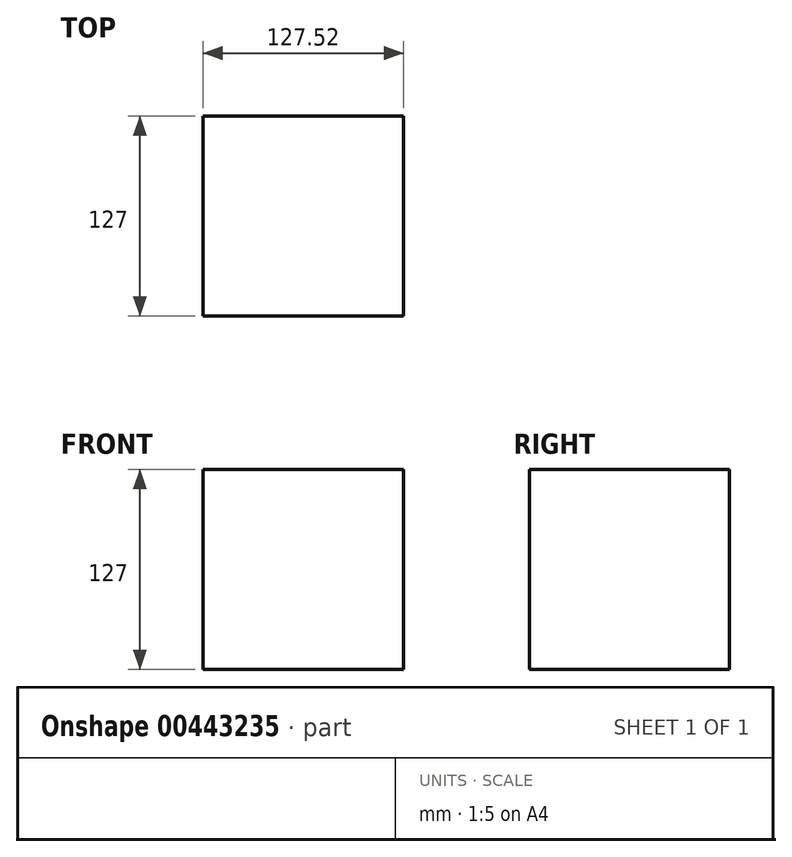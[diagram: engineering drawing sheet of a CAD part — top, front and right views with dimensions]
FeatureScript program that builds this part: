
annotation { "Feature Type Name" : "Feature", "Feature Type Description" : "" }
export const myFeature = defineFeature(function(context is Context, id is Id, definition is map)
    precondition{}
    {
        {
            var Q0;
            Q0=qCreatedBy(makeId("Front.planeOp"),FACE);
            var sketch = newSketch(context, id + "F0", { "sketchPlane" : qUnion([Q0])});
            skLineSegment(sketch, "E0", {"start": v(-63.76, 63.5) * mm, "end": v(63.76, 63.5) * mm});
            skLineSegment(sketch, "E1", {"start": v(63.76, -63.5) * mm, "end": v(-63.76, -63.5) * mm});
            skLineSegment(sketch, "E2", {"start": v(-63.76, 63.5) * mm, "end": v(-63.76, -63.5) * mm});
            skLineSegment(sketch, "E3", {"start": v(63.76, 63.5) * mm, "end": v(63.76, -63.5) * mm});
            skSolve(sketch);
        }
        {
            var Q0;
            Q0=makeQuery(id+"F0.imprint","IMPRINT",FACE,{"disambiguationData":[TD([[makeQuery(id+"F0.imprint","IMPRINT",EDGE,{"derivedFrom":sQuery(id+"F0.wireOp",EDGE,"E0")}),-1.0]])]});
            extrude(context, id + "F1", {"entities" : qUnion([Q0]), "endBound" : BoundingType.SYMMETRIC, "depth" : 127 * mm});
        }
    });
